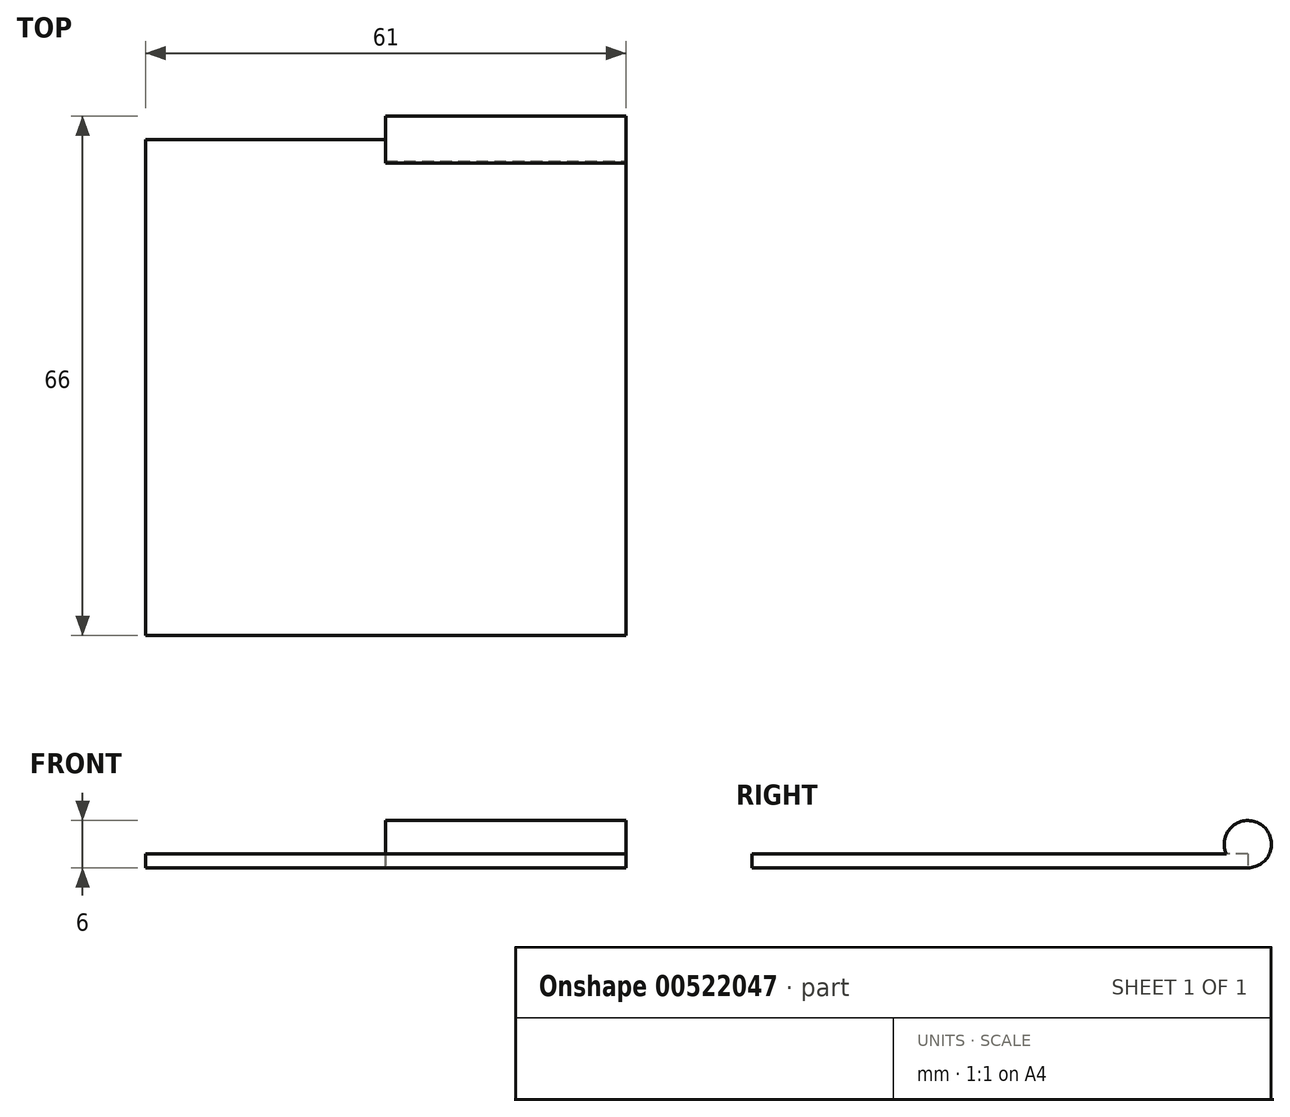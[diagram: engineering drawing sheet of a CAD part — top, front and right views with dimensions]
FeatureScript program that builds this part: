
annotation { "Feature Type Name" : "Feature", "Feature Type Description" : "" }
export const myFeature = defineFeature(function(context is Context, id is Id, definition is map)
    precondition{}
    {
        {
            var Q0;
            Q0=qCreatedBy(makeId("Top.planeOp"),FACE);
            var sketch = newSketch(context, id + "F0", { "sketchPlane" : qUnion([Q0])});
            skLineSegment(sketch, "E0.bottom", {"start": v(0, 0) * mm, "end": v(61, 0) * mm});
            skLineSegment(sketch, "E0.top", {"start": v(0, -63) * mm, "end": v(61, -63) * mm});
            skLineSegment(sketch, "E0.left", {"start": v(0, 0) * mm, "end": v(0, -63) * mm});
            skLineSegment(sketch, "E0.right", {"start": v(61, 0) * mm, "end": v(61, -63) * mm});
            skSolve(sketch);
        }
        {
            var Q0;
            Q0=makeQuery(id+"F0.imprint","IMPRINT",FACE,{"disambiguationData":[TD([[makeQuery(id+"F0.imprint","IMPRINT",EDGE,{"derivedFrom":sQuery(id+"F0.wireOp",EDGE,"E0.bottom")}),-1.0]])]});
            extrude(context, id + "F1", {"entities" : qUnion([Q0]), "depth" : 1.8 * mm, "offsetDistance" : 25 * mm});
        }
        {
            var Q0;
            Q0=makeQuery(id+"F1.opExtrude","SWEPT_FACE",FACE,{"disambiguationData":[OSD([sQuery(id+"F0.wireOp",EDGE,"E0.right")])]});
            var sketch = newSketch(context, id + "F2", { "sketchPlane" : qUnion([Q0])});
            skCircle(sketch, "E1", {"center": v(0, 3) * mm, "radius": 3 * mm});
            skSolve(sketch);
        }
        {
            var Q0;
            {var subQ1=sQuery(id+"F0.wireOp",EDGE,"E0.right");var subQ2=makeQuery(id+"F1.opExtrude","SWEPT_EDGE",EDGE,{"disambiguationData":[OSD([sQuery(id+"F0.wireOp",EDGE,"E0.bottom"),subQ1])]});Q0=makeQuery(id+"F2.imprint","IMPRINT",FACE,{"disambiguationData":[TD([[makeQuery(id+"F2.imprint","IMPRINT",EDGE,{"derivedFrom":subQ2}),1.0]])]});}
            extrude(context, id + "F3", {"entities" : qUnion([Q0]), "operationType" : NewBodyOperationType.ADD, "oppositeDirection" : true, "depth" : (61 / 2) * mm, "offsetDistance" : 25 * mm});
        }
    });
